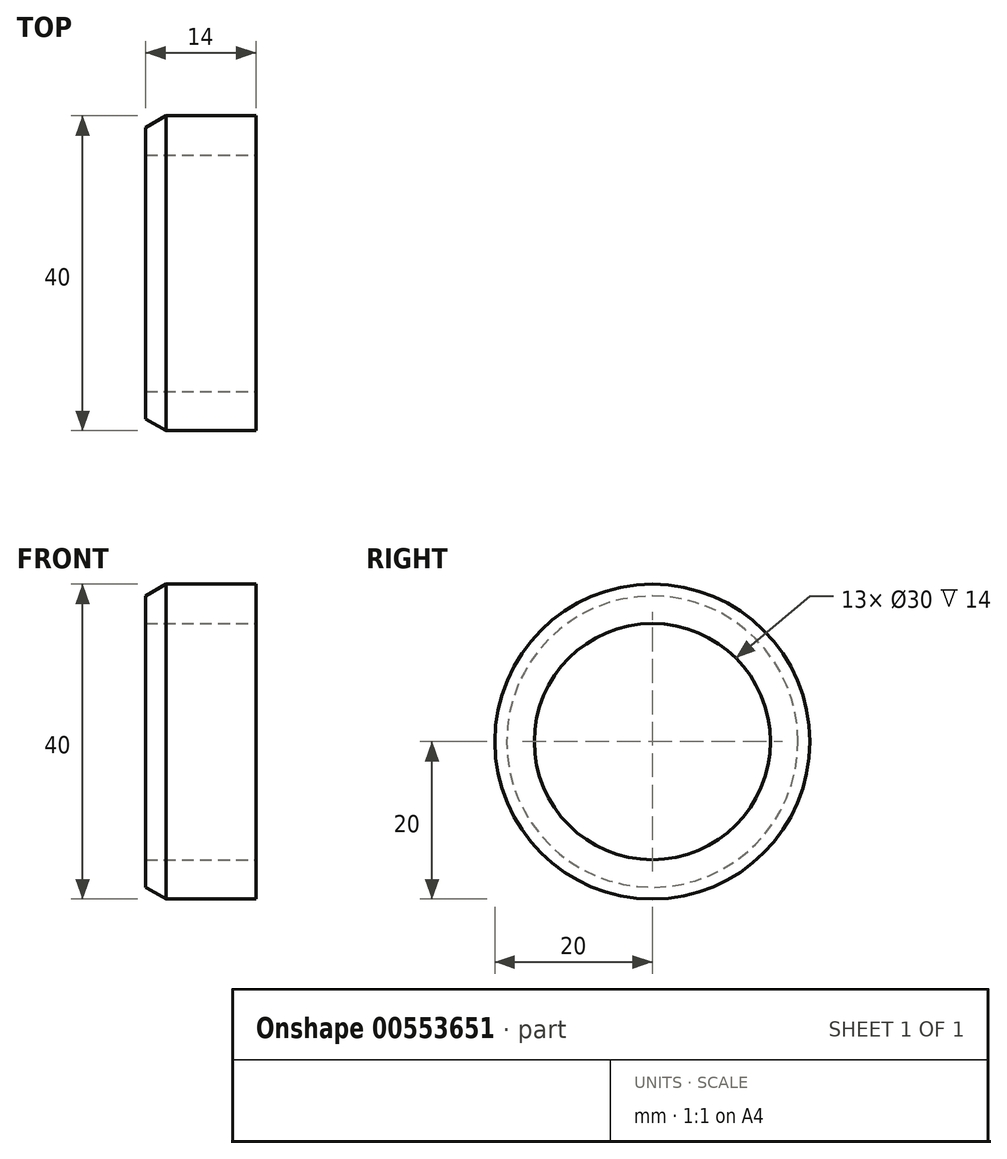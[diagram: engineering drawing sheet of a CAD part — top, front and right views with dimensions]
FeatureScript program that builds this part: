
annotation { "Feature Type Name" : "Feature", "Feature Type Description" : "" }
export const myFeature = defineFeature(function(context is Context, id is Id, definition is map)
    precondition{}
    {
        {
            var Q0;
            Q0=qCreatedBy(makeId("Front.planeOp"),FACE);
            var sketch = newSketch(context, id + "F0", { "sketchPlane" : qUnion([Q0])});
            skLineSegment(sketch, "E0", {"start": v(0, 20) * mm, "end": v(-11.4, 20) * mm});
            skLineSegment(sketch, "E1", {"start": v(-11.4, 20) * mm, "end": v(-14, 18.5) * mm});
            skLineSegment(sketch, "E2", {"start": v(-14, 18.5) * mm, "end": v(-14, 15) * mm});
            skLineSegment(sketch, "E3", {"start": v(-14, 15) * mm, "end": v(0, 15) * mm});
            skLineSegment(sketch, "E4", {"start": v(0, 15) * mm, "end": v(0, 20) * mm});
            skLineSegment(sketch, "E5", {"start": v(0, 0) * mm, "end": v(-14, 0) * mm, "construction": true});
            skSolve(sketch);
        }
        {
            var Q0;
            Q0=qSketchRegion(id+"F0",true);
            var Q1;
            Q1=sQuery(id+"F0.wireOp",EDGE,"E5");
            revolve(context, id + "F1", {"entities" : qUnion([Q0]), "axis" : qUnion([Q1]), "revolveType" : RevolveType.FULL});
        }
    });
